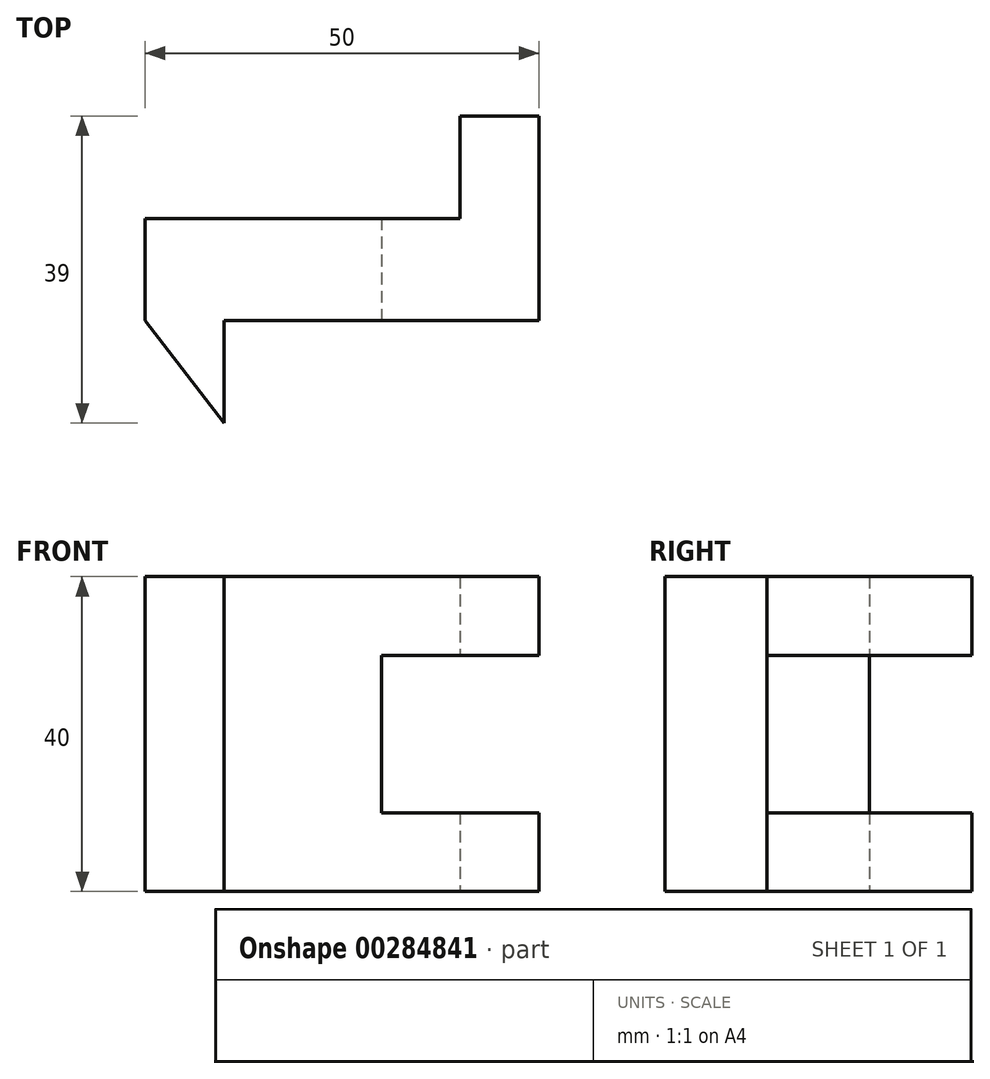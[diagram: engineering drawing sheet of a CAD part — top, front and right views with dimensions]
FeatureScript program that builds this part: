
annotation { "Feature Type Name" : "Feature", "Feature Type Description" : "" }
export const myFeature = defineFeature(function(context is Context, id is Id, definition is map)
    precondition{}
    {
        {
            var Q0;
            Q0=qCreatedBy(makeId("Top.planeOp"),FACE);
            var sketch = newSketch(context, id + "F0", { "sketchPlane" : qUnion([Q0])});
            skLineSegment(sketch, "E0.bottom", {"start": v(0, 0) * mm, "end": v(50, 0) * mm});
            skLineSegment(sketch, "E0.top", {"start": v(0, 39) * mm, "end": v(50, 39) * mm});
            skLineSegment(sketch, "E0.left", {"start": v(0, 0) * mm, "end": v(0, 39) * mm});
            skLineSegment(sketch, "E0.right", {"start": v(50, 0) * mm, "end": v(50, 39) * mm});
            skLineSegment(sketch, "E1", {"start": v(10, 0) * mm, "end": v(10, 13) * mm});
            skLineSegment(sketch, "E2", {"start": v(10, 13) * mm, "end": v(50, 13) * mm});
            skLineSegment(sketch, "E3", {"start": v(40, 39) * mm, "end": v(40, 26) * mm});
            skLineSegment(sketch, "E4", {"start": v(40, 26) * mm, "end": v(0, 26) * mm});
            skSolve(sketch);
        }
        {
            var Q0;
            {var subQ9=sQuery(id+"F0.wireOp",EDGE,"E1");Q0=makeQuery(id+"F0.imprint","IMPRINT",FACE,{"disambiguationData":[TD([[makeQuery(id+"F0.imprint","IMPRINT",EDGE,{"derivedFrom":subQ9}),1.0]])]});}
            extrude(context, id + "F1", {"entities" : qUnion([Q0]), "depth" : 40 * mm, "symmetric" : true});
        }
        {
            var Q0;
            Q0=makeQuery(id+"F1.opExtrude","SWEPT_FACE",FACE,{"disambiguationData":[OSD([sQuery(id+"F0.wireOp",EDGE,"E2")])]});
            var sketch = newSketch(context, id + "F2", { "sketchPlane" : qUnion([Q0])});
            skLineSegment(sketch, "E5.bottom", {"start": v(50, 10) * mm, "end": v(30, 10) * mm});
            skLineSegment(sketch, "E5.top", {"start": v(50, -10) * mm, "end": v(30, -10) * mm});
            skLineSegment(sketch, "E5.left", {"start": v(50, 10) * mm, "end": v(50, -10) * mm});
            skLineSegment(sketch, "E5.right", {"start": v(30, 10) * mm, "end": v(30, -10) * mm});
            skSolve(sketch);
        }
        {
            var Q0;
            Q0=qSketchRegion(id+"F2",true);
            extrude(context, id + "F3", {"entities" : qUnion([Q0]), "operationType" : NewBodyOperationType.REMOVE, "endBound" : BoundingType.THROUGH_ALL, "oppositeDirection" : true, "depth" : 25 * mm});
        }
        {
            var Q0;
            Q0=makeQuery(id+"F1.opExtrude","CAP_FACE",FACE,{"disambiguationData":[OSD([sQuery(id+"F0.wireOp",EDGE,"E0.bottom"),sQuery(id+"F0.wireOp",EDGE,"E0.top"),sQuery(id+"F0.wireOp",EDGE,"E0.left"),sQuery(id+"F0.wireOp",EDGE,"E0.right"),sQuery(id+"F0.wireOp",EDGE,"E1"),sQuery(id+"F0.wireOp",EDGE,"E2"),sQuery(id+"F0.wireOp",EDGE,"E3"),sQuery(id+"F0.wireOp",EDGE,"E4")])],"isStart":false});
            var sketch = newSketch(context, id + "F4", { "sketchPlane" : qUnion([Q0])});
            skLineSegment(sketch, "E6", {"start": v(10, 0) * mm, "end": v(0, 13) * mm});
            skLineSegment(sketch, "E7", {"start": v(0, 13) * mm, "end": v(0, 0) * mm});
            skLineSegment(sketch, "E8", {"start": v(0, 0) * mm, "end": v(10, 0) * mm});
            skSolve(sketch);
        }
        {
            var Q0;
            Q0 = qSketchRegion(id + "F4", true);
            extrude(context, id + "F5", {"entities" : qUnion([Q0]), "operationType" : NewBodyOperationType.REMOVE, "endBound" : BoundingType.THROUGH_ALL, "oppositeDirection" : true, "depth" : 25 * mm});
        }
    });
